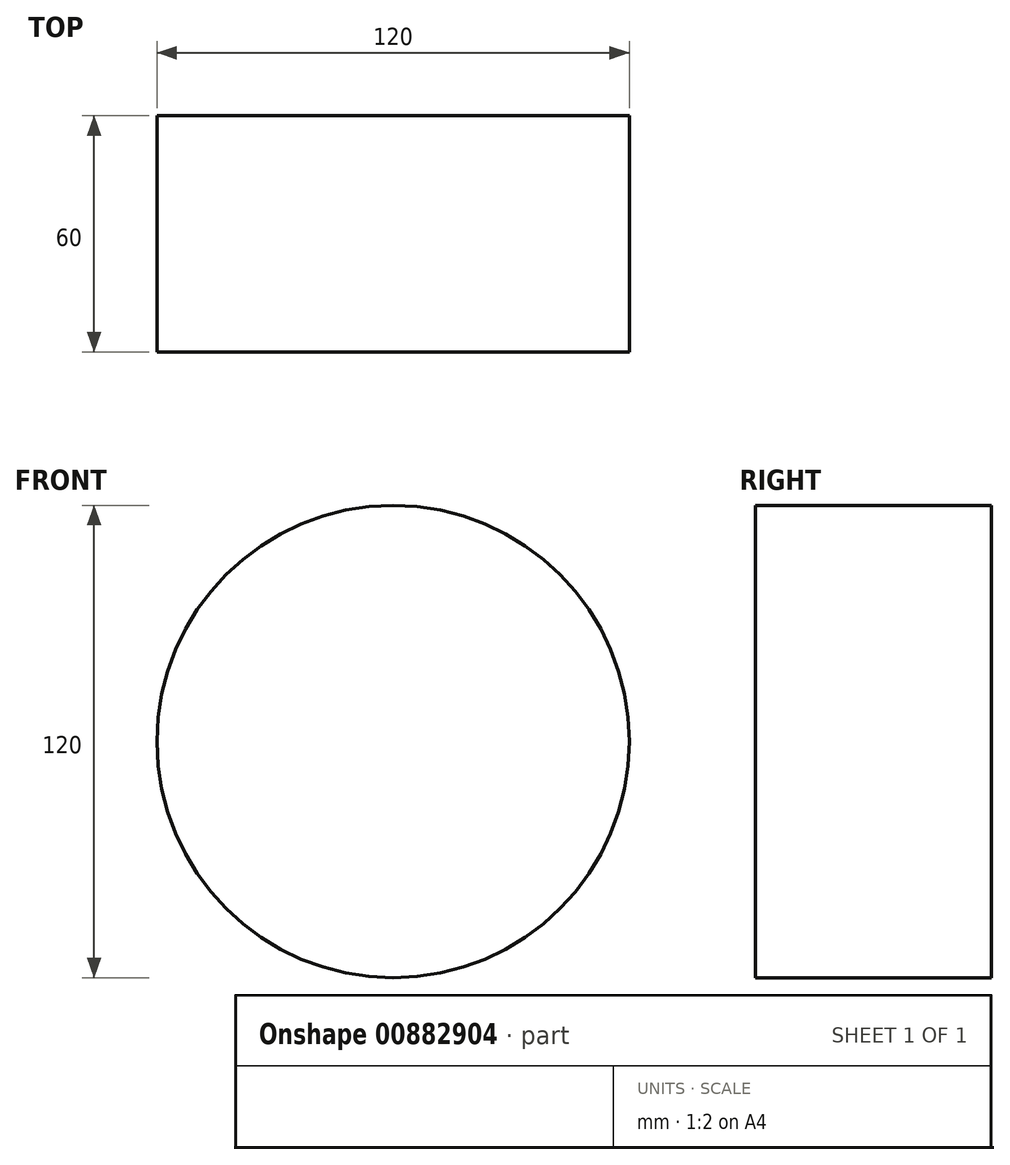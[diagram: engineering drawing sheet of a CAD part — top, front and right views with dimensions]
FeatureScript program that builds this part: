
annotation { "Feature Type Name" : "Feature", "Feature Type Description" : "" }
export const myFeature = defineFeature(function(context is Context, id is Id, definition is map)
    precondition{}
    {
        {
            var Q0;
            Q0=qCreatedBy(makeId("Front.planeOp"),FACE);
            var sketch = newSketch(context, id + "F0", { "sketchPlane" : qUnion([Q0])});
            skCircle(sketch, "E0", {"center": v(0, 0) * mm, "radius": 60 * mm});
            skSolve(sketch);
        }
        {
            var Q0;
            Q0 = qSketchRegion(id + "F0", true);
            extrude(context, id + "F1", {"entities" : qUnion([Q0]), "depth" : 60 * mm, "offsetDistance" : 25 * mm});
        }
    });
